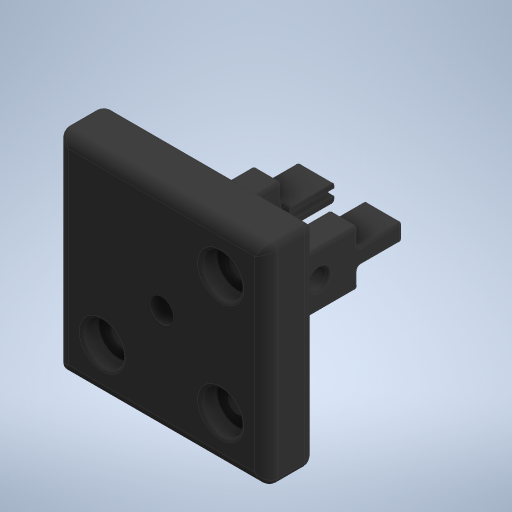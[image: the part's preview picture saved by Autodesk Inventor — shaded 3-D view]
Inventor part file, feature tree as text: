
AUTODESK INVENTOR PART (.ipt)
format: ipt  version: 2023.5 (Build 275446020, 446B)  size: 1,076,224 bytes
history: native  units: mm
features: other x13, extrude x13, fillet x6, chamfer x4, mirror x1, projected_geometry x1
ambient origin geometry x8: Origin, YZ Plane, XZ Plane, XY Plane, X Axis, Y Axis, Z Axis, Center Point
bodies: Solid1 (feature_tree)
feature tree (38):
  other  "NP2_Payload.ipt"
  other  "Universal_ConstructorHead.ipt"
  other  "Sk:SideArmSlot"
  extrude  "Ex:SideArmSlot"  Depth=10.0mm
  extrude  "Ex:SideArmExtension"  Depth=8.0mm TaperAngle=0.0deg
  other  "Sk:LateralFeatures"
  extrude  "Ex:TopConnection"  Depth=20.0mm TaperAngle=0.0deg
  extrude  "Ex:ThreadProtrusion"  TaperAngle=0.0deg  [1 undecoded]
  fillet  "Fillet:Protrusion"  [1 undecoded]
  fillet  "Fillet:AllOfArm"  Radius=3.16mm
  extrude  "Ex:ScrewHole"  Depth=1.16mm
  extrude  "Ex:InterArmExtend"  Depth=6.5mm
  other  "Move:InterArmExtend"
  mirror  "Mirror1"
  extrude  "Ex:ThreadInsert"  Depth=1.0mm
  chamfer  "Chamfer:ThreadInsertOpt1"  Distance=10.0mm
  chamfer  "Chamfer:ThreadInsertOpt2"  Distance=6.0mm
  fillet  "Fillet:ThroughHoleOpt1"  Radius=9.0mm
  fillet  "Fillet:ThroughHoleOpt2"  Radius=10.0mm
  other  "TopPlane"
  other  "Sk:TopExpansion"
  fillet  "Fillet:TopCorner"  Radius=3.0mm
  extrude  "Ex:MainTopBody"  Depth=6.5mm
  extrude  "Ex:CavitiesForPosts"  Depth=6.5mm
  extrude  "Ex:TopThread1"  Depth=6.5mm
  chamfer  "Chamfer:TopThread1"  Distance=5.0mm
  extrude  "Ex:PostThroughHoles"  Depth=10.0mm
  extrude  "Ex:ScrewRecesses"  TaperAngle=0.0deg  [1 undecoded]
  extrude  "Ex:TopThread2"  Depth=5.0mm
  chamfer  "Chamfer:TopThread2"  Distance=15.0mm
  fillet  "Fillet:Final"  Radius=8.0mm
  other  "TaggingFeature1"
  other  "TaggingFeature2"
  projected_geometry  "Projected Loop6"
  other  "Solid1::NP2_Payload.ipt"
  other  "Srf1"
  other  "Solid1::Universal_ConstructorHead.ipt"
  other  "Srf2"
note: 3 required parameter values undecoded (feature->parameter linkage not recoverable at this tier; creation-order binding heuristic only, values carry confidence <= 0.55)
